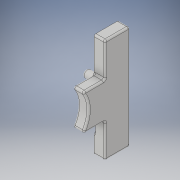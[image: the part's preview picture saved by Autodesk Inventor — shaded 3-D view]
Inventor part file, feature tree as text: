
AUTODESK INVENTOR PART (.ipt)
format: ipt  version: 2018 (Build 220112000, 112)  size: 386,048 bytes
history: native  units: in
note: dims shown in document units (in); Inventor stores cm internally (conversion verified against a paired STEP export)
features: reference x23, sketch x15, extrude x14, other x9, fillet x5, projected_geometry x3
ambient origin geometry x8: Origin, YZ Plane, XZ Plane, XY Plane, X Axis, Y Axis, Z Axis, Center Point
bodies: Solid1 (feature_tree)
feature tree (69):
  extrude  "Extrusion1"  Depth=0.125in
  extrude  "Extrusion2"  Depth=0.4724in TaperAngle=0.0deg
  sketch  "Sketch3"  dims[d5=0.0787in d6=0.0in d7=0.2in d8=0.0in]
  extrude  "Extrusion3"  Depth=0.0787in TaperAngle=0.0deg
  extrude  "Extrusion4"  Depth=0.4in
  extrude  "Extrusion5"  Depth=0.25in
  extrude  "Extrusion6"  Depth=0.0787in TaperAngle=0.0deg
  extrude  "Extrusion7"  Depth=0.1181in
  extrude  "Extrusion8"  Depth=0.1181in
  extrude  "Extrusion10"  Depth=0.0787in TaperAngle=0.0deg
  extrude  "Extrusion12"  Depth=0.25in TaperAngle=0.0deg
  fillet  "Fillet2"  Radius=0.75in
  fillet  "Fillet3"  Radius=0.75in
  extrude  "Extrusion13"  Depth=0.0394in
  fillet  "Fillet4"  Radius=1.0in
  fillet  "Fillet6"  Radius=0.0394in
  extrude  "Extrusion14"  Depth=0.0394in
  fillet  "Fillet8"  Radius=1.0in
  extrude  "Extrusion15"  Depth=0.0394in
  extrude  "Extrusion16"  Depth=0.0394in
  sketch  "Sketch1"  dims[d0=0.5in d1=0.125in]
  reference  "Reference1"
  reference  "Reference2"
  reference  "Reference3"
  reference  "Reference4"
  reference  "Reference5"
  reference  "Reference6"
  reference  "Reference7"
  reference  "Reference8"
  reference  "Reference9"
  reference  "Reference10"
  reference  "Reference11"
  reference  "Reference12"
  reference  "Reference13"
  reference  "Reference14"
  reference  "Reference15"
  reference  "Reference16"
  reference  "Reference17"
  sketch  "Sketch2"  dims[d2=0.7in d3=0.4724in d4=0.0in]
  projected_geometry  "Projected Loop1"
  projected_geometry  "Projected Loop2"
  reference  "Reference18"
  reference  "Reference19"
  sketch  "Sketch4"  dims[d9=0.4in d10=0.4in]
  projected_geometry  "Projected Loop3"
  sketch  "Sketch5"  dims[d11=0.5512in d12=0.0in d13=0.25in]
  reference  "Reference20"
  sketch  "Sketch6"  dims[d14=0.25in d15=0.0787in d16=0.0in]
  sketch  "Sketch7"  dims[d17=0.125in d18=0.1181in]
  sketch  "Sketch8"  dims[d19=0.125in d20=0.1181in]
  reference  "Reference21"
  sketch  "Sketch9"  dims[d21=1.15in d22=0.0787in d23=0.0in]
  sketch  "Sketch11"  dims[d24=1.0in d25=0.0in d26=0.25in d27=0.0in d31=0.75in d32=0.75in]
  reference  "Reference23"
  sketch  "Sketch13"  dims[d33=0.5in d34=0.0in d38=0.1575in d39=1.0in d40=0.0in d42=0.0394in]
  reference  "Reference25"
  sketch  "Sketch14"  dims[d43=0.0394in d44=0.65in d45=1.0in d46=0.0in]
  sketch  "Sketch15"  dims[d47=0.0394in d49=0.0394in]
  sketch  "Sketch16"  dims[d51=0.0098in d52=0.0in d53=0.0394in]
  sketch  "Sketch17"  dims[d54=1.0in d55=0.0in d56=0.0098in d57=0.0in]
  other  "<userpath>\OneDrive\Documents\Inventor\TSA\2018\Animatronics\Tortoise\AssemblyTURTLE.iam"
  other  "AssemblyTURTLE.iam"
  other  "servo (2):1"
  other  "smallergear:1"
  other  "Frame:1"
  other  "<userpath>\OneDrive\Documents\Inventor\TSA\2018\Animatronics\Tortoise\TurtleAssembly.iam"
  other  "TurtleAssembly.iam"
  other  "smallergear:3"
  other  "holder_gear_mount:1"
